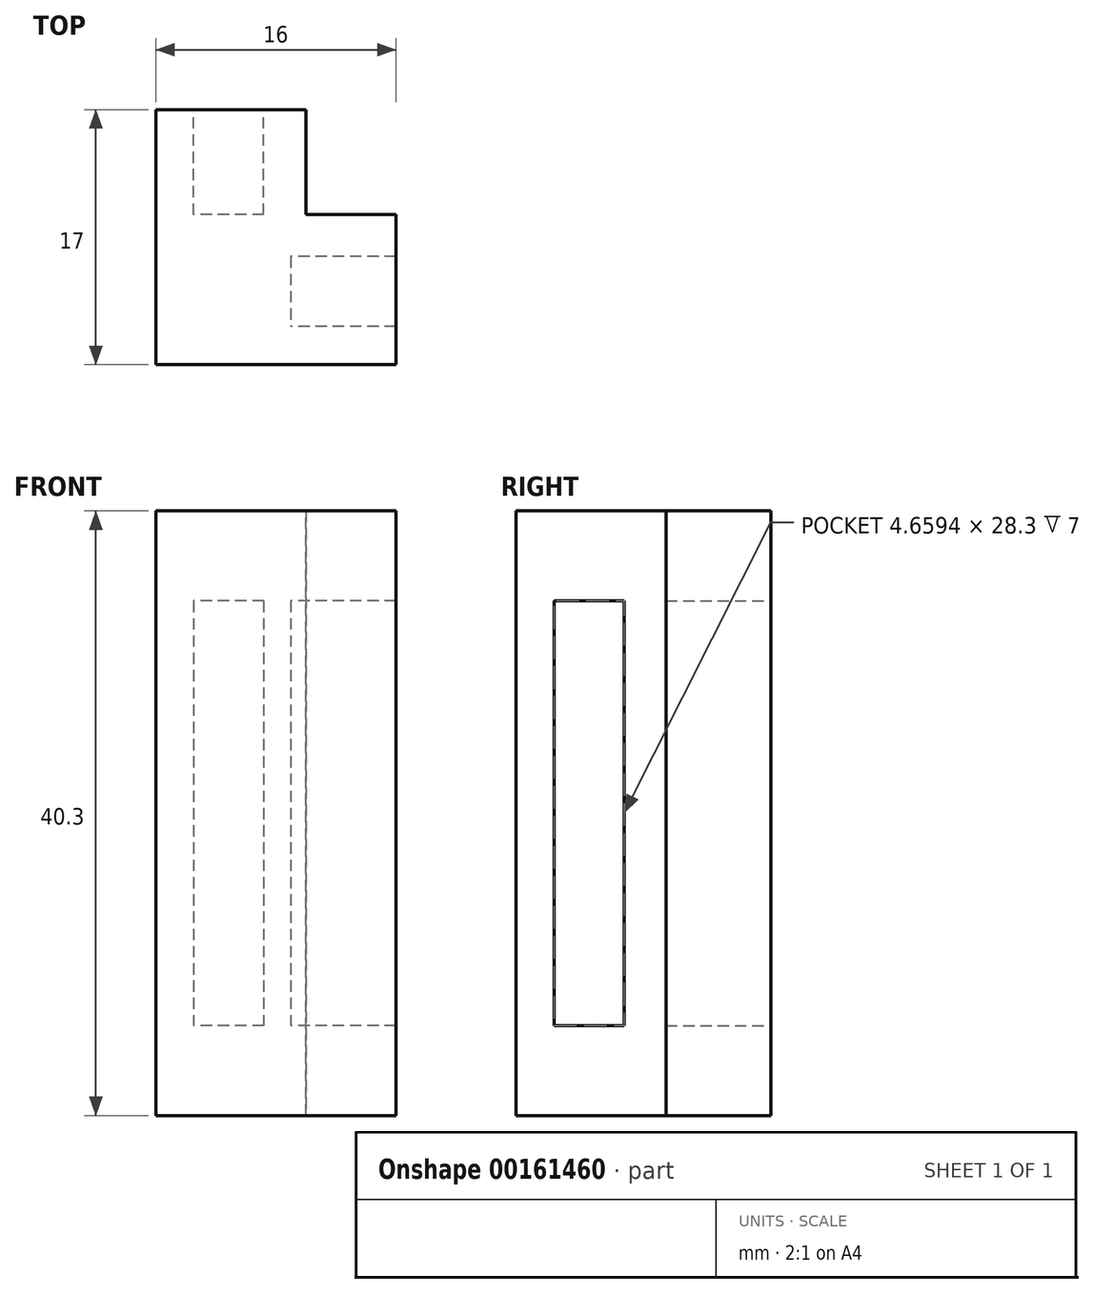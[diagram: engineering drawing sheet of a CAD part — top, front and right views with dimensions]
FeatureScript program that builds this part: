
annotation { "Feature Type Name" : "Feature", "Feature Type Description" : "" }
export const myFeature = defineFeature(function(context is Context, id is Id, definition is map)
    precondition{}
    {
        {
            var Q0;
            Q0=qCreatedBy(makeId("Front.planeOp"),FACE);
            var sketch = newSketch(context, id + "F0", { "sketchPlane" : qUnion([Q0])});
            skLineSegment(sketch, "E0.bottom", {"start": v(-30.25, -40.58) * mm, "end": v(-20.25, -40.58) * mm});
            skLineSegment(sketch, "E0.top", {"start": v(-30.25, -80.88) * mm, "end": v(-20.25, -80.88) * mm});
            skLineSegment(sketch, "E0.left", {"start": v(-30.25, -40.58) * mm, "end": v(-30.25, -80.88) * mm});
            skLineSegment(sketch, "E0.right", {"start": v(-20.25, -40.58) * mm, "end": v(-20.25, -80.88) * mm});
            skLineSegment(sketch, "E1.bottom", {"start": v(-23.06, -46.58) * mm, "end": v(-27.72, -46.58) * mm});
            skLineSegment(sketch, "E1.top", {"start": v(-23.06, -74.88) * mm, "end": v(-27.72, -74.88) * mm});
            skLineSegment(sketch, "E1.left", {"start": v(-23.06, -46.58) * mm, "end": v(-23.06, -74.88) * mm});
            skLineSegment(sketch, "E1.right", {"start": v(-27.72, -46.58) * mm, "end": v(-27.72, -74.88) * mm});
            skLineSegment(sketch, "E2", {"start": v(-23.06, -74.88) * mm, "end": v(-23.06, -80.88) * mm, "construction": true});
            skLineSegment(sketch, "E3", {"start": v(-27.72, -46.58) * mm, "end": v(-27.72, -40.58) * mm, "construction": true});
            skSolve(sketch);
        }
        {
            var Q0;
            Q0=makeQuery(id+"F0.imprint","IMPRINT",FACE,{"disambiguationData":[TD([[makeQuery(id+"F0.imprint","IMPRINT",EDGE,{"derivedFrom":sQuery(id+"F0.wireOp",EDGE,"E0.bottom")}),-1.0]])]});
            var Q1;
            Q1=makeQuery(id+"F0.imprint","IMPRINT",FACE,{"disambiguationData":[TD([[makeQuery(id+"F0.imprint","IMPRINT",EDGE,{"derivedFrom":sQuery(id+"F0.wireOp",EDGE,"0H4b4fvO-dyxi-FZrW-pJNc-f5h2Ua2qFgm1.bottom")}),-1.0]])]});
            var Q2;
            Q2=makeQuery(id+"F0.imprint","IMPRINT",FACE,{"disambiguationData":[TD([[makeQuery(id+"F0.imprint","IMPRINT",EDGE,{"derivedFrom":sQuery(id+"F0.wireOp",EDGE,"RIwqPRcQ-8Yhb-SA2c-7hZh-BoyqNhFDoh6P.bottom")}),-1.0]])]});
            var Q3;
            Q3=makeQuery(id+"F0.imprint","IMPRINT",FACE,{"disambiguationData":[TD([[makeQuery(id+"F0.imprint","IMPRINT",EDGE,{"derivedFrom":sQuery(id+"F0.wireOp",EDGE,"V1CP0RN2-3pWF-4ICx-AOtc-XG8nw0NRMOAc.bottom")}),-1.0]])]});
            var Q4;
            Q4=makeQuery(id+"F0.imprint","IMPRINT",FACE,{"disambiguationData":[TD([[makeQuery(id+"F0.imprint","IMPRINT",EDGE,{"derivedFrom":sQuery(id+"F0.wireOp",EDGE,"E1.bottom")}),1.0]])]});
            extrude(context, id + "F1", {"entities" : qUnion([Q0, Q1, Q2, Q3, Q4]), "depth" : 17 * mm});
        }
        {
            var Q0;
            Q0=makeQuery(id+"F0.imprint","IMPRINT",FACE,{"disambiguationData":[TD([[makeQuery(id+"F0.imprint","IMPRINT",EDGE,{"derivedFrom":sQuery(id+"F0.wireOp",EDGE,"0H4b4fvO-dyxi-FZrW-pJNc-f5h2Ua2qFgm1.bottom")}),-1.0]])]});
            var Q1;
            Q1=makeQuery(id+"F0.imprint","IMPRINT",FACE,{"disambiguationData":[TD([[makeQuery(id+"F0.imprint","IMPRINT",EDGE,{"derivedFrom":sQuery(id+"F0.wireOp",EDGE,"RIwqPRcQ-8Yhb-SA2c-7hZh-BoyqNhFDoh6P.bottom")}),-1.0]])]});
            var Q2;
            Q2=makeQuery(id+"F0.imprint","IMPRINT",FACE,{"disambiguationData":[TD([[makeQuery(id+"F0.imprint","IMPRINT",EDGE,{"derivedFrom":sQuery(id+"F0.wireOp",EDGE,"V1CP0RN2-3pWF-4ICx-AOtc-XG8nw0NRMOAc.bottom")}),-1.0]])]});
            var Q3;
            Q3=makeQuery(id+"F0.imprint","IMPRINT",FACE,{"disambiguationData":[TD([[makeQuery(id+"F0.imprint","IMPRINT",EDGE,{"derivedFrom":sQuery(id+"F0.wireOp",EDGE,"E1.bottom")}),1.0]])]});
            extrude(context, id + "F2", {"entities" : qUnion([Q0, Q1, Q2, Q3]), "operationType" : NewBodyOperationType.REMOVE, "depth" : 7 * mm});
        }
        {
            var Q0;
            Q0=makeQuery(id+"F1.opExtrude","SWEPT_FACE",FACE,{"disambiguationData":[OSD([sQuery(id+"F0.wireOp",EDGE,"E0.right")])]});
            var sketch = newSketch(context, id + "F3", { "sketchPlane" : qUnion([Q0])});
            skLineSegment(sketch, "E4.bottom", {"start": v(-17, -40.58) * mm, "end": v(-7, -40.58) * mm});
            skLineSegment(sketch, "E4.top", {"start": v(-17, -80.88) * mm, "end": v(-7, -80.88) * mm});
            skLineSegment(sketch, "E4.left", {"start": v(-17, -40.58) * mm, "end": v(-17, -80.88) * mm});
            skLineSegment(sketch, "E4.right", {"start": v(-7, -40.58) * mm, "end": v(-7, -80.88) * mm});
            skLineSegment(sketch, "E5.bottom", {"start": v(-9.8, -46.58) * mm, "end": v(-14.46, -46.58) * mm});
            skLineSegment(sketch, "E5.top", {"start": v(-9.8, -74.88) * mm, "end": v(-14.46, -74.88) * mm});
            skLineSegment(sketch, "E5.left", {"start": v(-9.8, -46.58) * mm, "end": v(-9.8, -74.88) * mm});
            skLineSegment(sketch, "E5.right", {"start": v(-14.46, -46.58) * mm, "end": v(-14.46, -74.88) * mm});
            skLineSegment(sketch, "E6", {"start": v(-9.8, -74.88) * mm, "end": v(-9.8, -80.88) * mm, "construction": true});
            skLineSegment(sketch, "E7", {"start": v(-14.46, -46.58) * mm, "end": v(-14.46, -40.58) * mm, "construction": true});
            skSolve(sketch);
        }
        {
            var Q0;
            {var subQ1=sQuery(id+"F3.wireOp",EDGE,"E4.top");Q0=makeQuery(id+"F3.imprint","IMPRINT",FACE,{"disambiguationData":[TD([[makeQuery(id+"F3.imprint","IMPRINT",EDGE,{"derivedFrom":subQ1}),1.0]])]});}
            extrude(context, id + "F4", {"entities" : qUnion([Q0]), "operationType" : NewBodyOperationType.ADD, "depth" : 6 * mm, "hasSecondDirection" : true, "secondDirectionOppositeDirection" : true, "secondDirectionDepth" : 10 * mm});
        }
        {
            var Q0;
            Q0=makeQuery(id+"F3.imprint","IMPRINT",FACE,{"disambiguationData":[TD([[makeQuery(id+"F3.imprint","IMPRINT",EDGE,{"derivedFrom":sQuery(id+"F3.wireOp",EDGE,"E5.bottom")}),1.0]])]});
            extrude(context, id + "F5", {"entities" : qUnion([Q0]), "operationType" : NewBodyOperationType.REMOVE, "oppositeDirection" : true, "depth" : 1 * mm});
        }
    });
